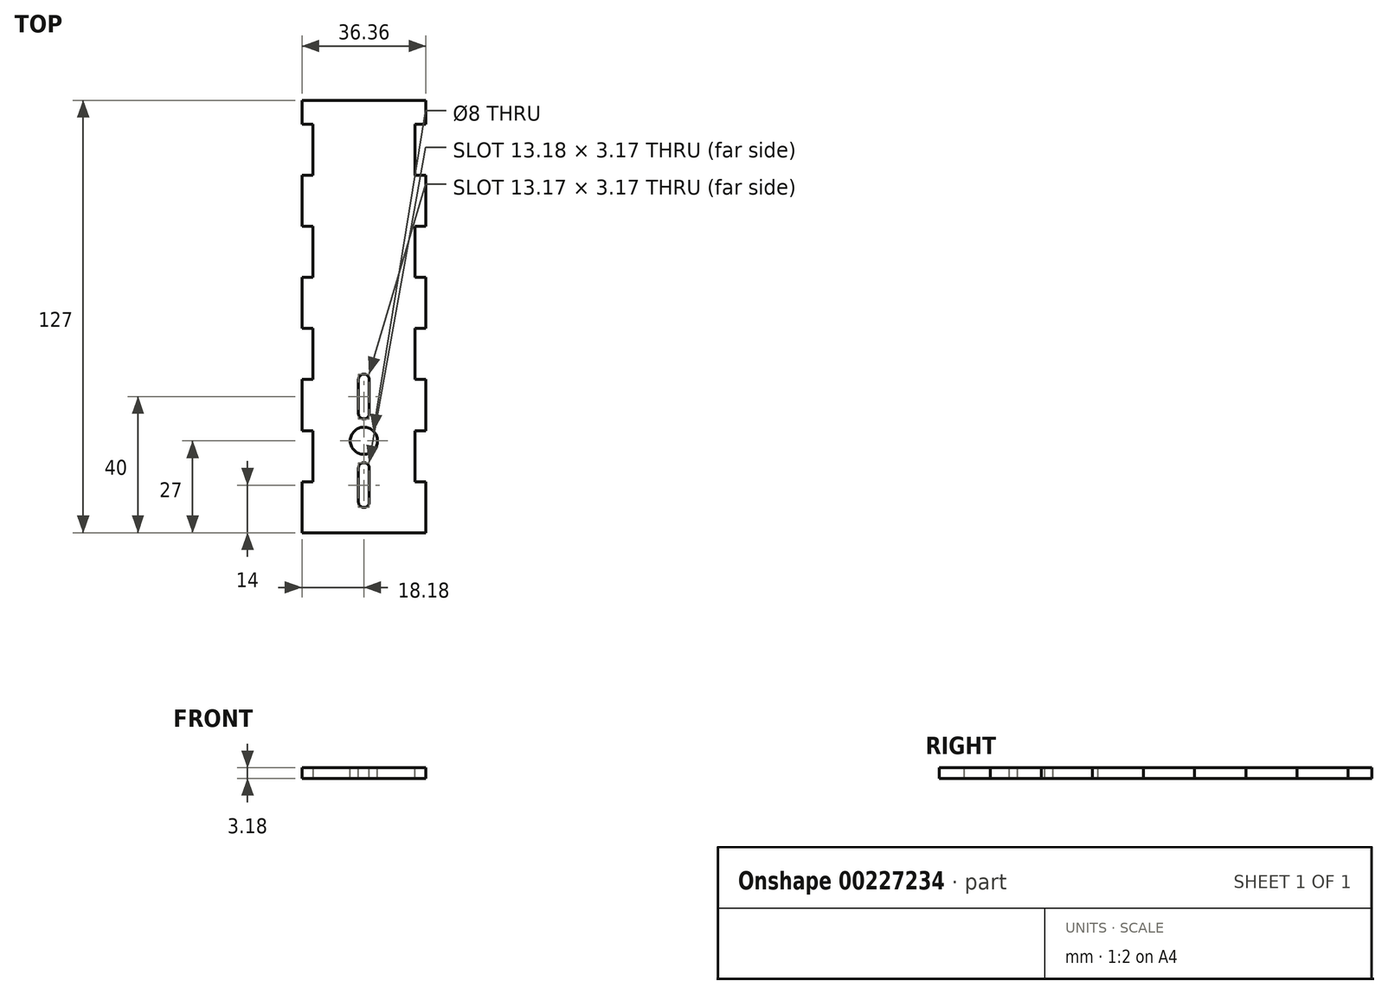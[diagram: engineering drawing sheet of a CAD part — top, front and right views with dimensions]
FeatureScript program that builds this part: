
annotation { "Feature Type Name" : "Feature", "Feature Type Description" : "" }
export const myFeature = defineFeature(function(context is Context, id is Id, definition is map)
    precondition{}
    {
        {
            var Q0;
            Q0=qCreatedBy(makeId("Top.planeOp"),FACE);
            var sketch = newSketch(context, id + "F0", { "sketchPlane" : qUnion([Q0])});
            skLineSegment(sketch, "E0.bottom", {"start": v(18.17, -41) * mm, "end": v(-18.17, -41) * mm});
            skLineSegment(sketch, "E0.top", {"start": v(18.18, 41) * mm, "end": v(-18.18, 41) * mm});
            skLineSegment(sketch, "E0.left", {"start": v(18.17, -41) * mm, "end": v(18.17, 41) * mm});
            skLineSegment(sketch, "E0.right", {"start": v(-18.17, -41) * mm, "end": v(-18.17, 41) * mm});
            skPoint(sketch, "E0.middle", {"position": v(0, 0) * mm});
            skLineSegment(sketch, "E1", {"start": v(-18.18, -26) * mm, "end": v(-15, -26) * mm});
            skLineSegment(sketch, "E2", {"start": v(-15, -26) * mm, "end": v(-15, -41) * mm});
            skLineSegment(sketch, "E3.MirrorCS", {"start": v(15, -26) * mm, "end": v(15, -41) * mm});
            skLineSegment(sketch, "E4.MirrorCS", {"start": v(18.18, -26) * mm, "end": v(15, -26) * mm});
            skLineSegment(sketch, "E5.0.1.0", {"start": v(-15, 4) * mm, "end": v(-15, -11) * mm});
            skLineSegment(sketch, "E5.0.1.1", {"start": v(-18.18, 4) * mm, "end": v(-15, 4) * mm});
            skLineSegment(sketch, "E5.0.1.2", {"start": v(18.18, 4) * mm, "end": v(15, 4) * mm});
            skLineSegment(sketch, "E5.0.1.3", {"start": v(15, 4) * mm, "end": v(15, -11) * mm});
            skLineSegment(sketch, "E5.0.2.0", {"start": v(-15, 34) * mm, "end": v(-15, 19) * mm});
            skLineSegment(sketch, "E5.0.2.1", {"start": v(-18.18, 34) * mm, "end": v(-15, 34) * mm});
            skLineSegment(sketch, "E5.0.2.2", {"start": v(18.18, 34) * mm, "end": v(15, 34) * mm});
            skLineSegment(sketch, "E5.0.2.3", {"start": v(15, 34) * mm, "end": v(15, 19) * mm});
            skLineSegment(sketch, "E5.direction1", {"start": v(-15, -41) * mm, "end": v(13.18, -41) * mm, "construction": true});
            skLineSegment(sketch, "E5.direction2", {"start": v(-15, -41) * mm, "end": v(-15, -11) * mm, "construction": true});
            skLineSegment(sketch, "E6", {"start": v(-15, -11) * mm, "end": v(-18.18, -11) * mm});
            skLineSegment(sketch, "E7", {"start": v(15, -11) * mm, "end": v(18.18, -11) * mm});
            skLineSegment(sketch, "E8", {"start": v(15, 19) * mm, "end": v(18.18, 19) * mm});
            skLineSegment(sketch, "E9", {"start": v(-15, 19) * mm, "end": v(-18.18, 19) * mm});
            skSolve(sketch);
        }
        {
            var Q0;
            {var subQ11=sQuery(id+"F0.wireOp",EDGE,"E0.top");Q0=makeQuery(id+"F0.imprint","IMPRINT",FACE,{"disambiguationData":[TD([[makeQuery(id+"F0.imprint","IMPRINT",EDGE,{"derivedFrom":subQ11}),1.0]])]});}
            extrude(context, id + "F1", {"entities" : qUnion([Q0]), "depth" : 3.17 * mm});
        }
        {
            var Q0;
            Q0=makeQuery(id+"F1.opExtrude","SWEPT_FACE",FACE,{"disambiguationData":[OSD([sQuery(id+"F0.wireOp",EDGE,"E0.bottom")])]});
            extrude(context, id + "F2", {"entities" : qUnion([Q0]), "operationType" : NewBodyOperationType.ADD, "depth" : 45 * mm});
        }
        {
            var Q0;
            Q0=makeQuery(id+"F1.opExtrude","CAP_FACE",FACE,{"disambiguationData":[OSD([sQuery(id+"F0.wireOp",EDGE,"E0.bottom"),sQuery(id+"F0.wireOp",EDGE,"E0.top"),sQuery(id+"F0.wireOp",EDGE,"E0.left"),sQuery(id+"F0.wireOp",EDGE,"E0.right"),sQuery(id+"F0.wireOp",EDGE,"E1"),sQuery(id+"F0.wireOp",EDGE,"E2"),sQuery(id+"F0.wireOp",EDGE,"E3.MirrorCS"),sQuery(id+"F0.wireOp",EDGE,"E4.MirrorCS"),sQuery(id+"F0.wireOp",EDGE,"E5.0.1.0"),sQuery(id+"F0.wireOp",EDGE,"E5.0.1.1"),sQuery(id+"F0.wireOp",EDGE,"E5.0.1.2"),sQuery(id+"F0.wireOp",EDGE,"E5.0.1.3"),sQuery(id+"F0.wireOp",EDGE,"E5.0.2.0"),sQuery(id+"F0.wireOp",EDGE,"E5.0.2.1"),sQuery(id+"F0.wireOp",EDGE,"E5.0.2.2"),sQuery(id+"F0.wireOp",EDGE,"E5.0.2.3"),sQuery(id+"F0.wireOp",EDGE,"E6"),sQuery(id+"F0.wireOp",EDGE,"E7"),sQuery(id+"F0.wireOp",EDGE,"E8"),sQuery(id+"F0.wireOp",EDGE,"E9")])],"isStart":false});
            var sketch = newSketch(context, id + "F3", { "sketchPlane" : qUnion([Q0])});
            skCircle(sketch, "E10", {"center": v(0, -59) * mm, "radius": 4 * mm});
            skLineSegment(sketch, "E11.bottom", {"start": v(1.59, -51) * mm, "end": v(-1.59, -51) * mm});
            skLineSegment(sketch, "E11.top", {"start": v(1.59, -41) * mm, "end": v(-1.59, -41) * mm});
            skLineSegment(sketch, "E11.left", {"start": v(1.59, -51) * mm, "end": v(1.59, -41) * mm});
            skLineSegment(sketch, "E11.right", {"start": v(-1.59, -51) * mm, "end": v(-1.59, -41) * mm});
            skPoint(sketch, "E11.middle", {"position": v(0, -46) * mm});
            skArc(sketch, "E12", {"start": v(1.59, -41) * mm, "mid": v(0, -39.41) * mm, "end": v(-1.59, -41) * mm});
            skArc(sketch, "E13", {"start": v(-1.59, -51) * mm, "mid": v(0, -52.59) * mm, "end": v(1.59, -51) * mm});
            skLineSegment(sketch, "E14", {"start": v(0, -59) * mm, "end": v(3.24, -59) * mm, "construction": true});
            skLineSegment(sketch, "E15.MirrorCS", {"start": v(1.59, -77) * mm, "end": v(-1.59, -77) * mm});
            skLineSegment(sketch, "E16.MirrorCS", {"start": v(1.59, -67) * mm, "end": v(-1.59, -67) * mm});
            skArc(sketch, "E17.MirrorCS", {"start": v(-1.59, -67) * mm, "mid": v(0, -65.41) * mm, "end": v(1.59, -67) * mm});
            skArc(sketch, "E18.MirrorCS", {"start": v(1.59, -77) * mm, "mid": v(0, -78.59) * mm, "end": v(-1.59, -77) * mm});
            skLineSegment(sketch, "E19.MirrorCS", {"start": v(1.59, -67) * mm, "end": v(1.59, -77) * mm});
            skLineSegment(sketch, "E20.MirrorCS", {"start": v(-1.59, -67) * mm, "end": v(-1.59, -77) * mm});
            skPoint(sketch, "E21.MirrorP", {"position": v(0, -72) * mm});
            skSolve(sketch);
        }
        {
            var Q0;
            Q0 = qSketchRegion(id + "F3", true);
            extrude(context, id + "F4", {"entities" : qUnion([Q0]), "operationType" : NewBodyOperationType.REMOVE, "oppositeDirection" : true, "depth" : 25 * mm});
        }
        {
            var Q0;
            {var subQ0=sQuery(id+"F0.wireOp",EDGE,"E3.MirrorCS");Q0=makeQuery(id+"F2.boolean.opBoolean","MERGE",FACE,{"derivedFrom":[makeQuery(id+"F1.opExtrude","SWEPT_FACE",FACE,{"disambiguationData":[OSD([subQ0])]}),makeQuery(id+"F2.opExtrude","SWEPT_FACE",FACE,{"disambiguationData":[OSD([sQuery(id+"F0.wireOp",EDGE,"E0.bottom"),subQ0])]})]});}
            var sketch = newSketch(context, id + "F5", { "sketchPlane" : qUnion([Q0])});
            skLineSegment(sketch, "E22.bottom", {"start": v(-41, 0) * mm, "end": v(-56, 0) * mm});
            skLineSegment(sketch, "E22.top", {"start": v(-41, 3.17) * mm, "end": v(-56, 3.17) * mm});
            skLineSegment(sketch, "E22.left", {"start": v(-41, 0) * mm, "end": v(-41, 3.18) * mm});
            skLineSegment(sketch, "E22.right", {"start": v(-56, 0) * mm, "end": v(-56, 3.17) * mm});
            skLineSegment(sketch, "E23.1.0.0", {"start": v(-86, 0) * mm, "end": v(-86, 3.17) * mm});
            skLineSegment(sketch, "E23.1.0.1", {"start": v(-71, 0) * mm, "end": v(-71, 3.18) * mm});
            skLineSegment(sketch, "E23.direction1", {"start": v(-56, 0) * mm, "end": v(-86, 0) * mm, "construction": true});
            skSolve(sketch);
        }
        {
            var Q0;
            {var subQ0=sQuery(id+"F5.wireOp",EDGE,"E23.1.0.0");Q0=makeQuery(id+"F5.imprint","IMPRINT",FACE,{"disambiguationData":[TD([[makeQuery(id+"F5.imprint","IMPRINT",EDGE,{"derivedFrom":subQ0}),1.0]])]});}
            var Q1;
            Q1=makeQuery(id+"F5.imprint","IMPRINT",FACE,{"disambiguationData":[TD([[makeQuery(id+"F5.imprint","IMPRINT",EDGE,{"derivedFrom":sQuery(id+"F5.wireOp",EDGE,"E22.bottom")}),-1.0]])]});
            extrude(context, id + "F6", {"entities" : qUnion([Q0, Q1]), "operationType" : NewBodyOperationType.ADD, "depth" : 3.17 * mm});
        }
        {
            var Q0;
            {var subQ0=sQuery(id+"F0.wireOp",EDGE,"E2");Q0=makeQuery(id+"F2.boolean.opBoolean","MERGE",FACE,{"derivedFrom":[makeQuery(id+"F1.opExtrude","SWEPT_FACE",FACE,{"disambiguationData":[OSD([subQ0])]}),makeQuery(id+"F2.opExtrude","SWEPT_FACE",FACE,{"disambiguationData":[OSD([sQuery(id+"F0.wireOp",EDGE,"E0.bottom"),subQ0])]})]});}
            var sketch = newSketch(context, id + "F7", { "sketchPlane" : qUnion([Q0])});
            skLineSegment(sketch, "E24.bottom", {"start": v(41, 3.17) * mm, "end": v(56, 3.17) * mm});
            skLineSegment(sketch, "E24.top", {"start": v(41, 0) * mm, "end": v(56, 0) * mm});
            skLineSegment(sketch, "E24.left", {"start": v(41, 3.17) * mm, "end": v(41, 0) * mm});
            skLineSegment(sketch, "E24.right", {"start": v(56, 3.17) * mm, "end": v(56, 0) * mm});
            skLineSegment(sketch, "E25.1.0.0", {"start": v(71, 3.17) * mm, "end": v(71, 0) * mm});
            skLineSegment(sketch, "E25.1.0.1", {"start": v(86, 3.17) * mm, "end": v(86, 0) * mm});
            skLineSegment(sketch, "E25.direction1", {"start": v(41, 0) * mm, "end": v(71, 0) * mm, "construction": true});
            skSolve(sketch);
        }
        {
            var Q0;
            Q0=makeQuery(id+"F7.imprint","IMPRINT",FACE,{"disambiguationData":[TD([[makeQuery(id+"F7.imprint","IMPRINT",EDGE,{"derivedFrom":sQuery(id+"F7.wireOp",EDGE,"E24.bottom")}),-1.0]])]});
            var Q1;
            {var subQ0=sQuery(id+"F7.wireOp",EDGE,"E25.1.0.0");Q1=makeQuery(id+"F7.imprint","IMPRINT",FACE,{"disambiguationData":[TD([[makeQuery(id+"F7.imprint","IMPRINT",EDGE,{"derivedFrom":subQ0}),1.0]])]});}
            extrude(context, id + "F8", {"entities" : qUnion([Q0, Q1]), "operationType" : NewBodyOperationType.ADD, "depth" : 3.17 * mm});
        }
    });
